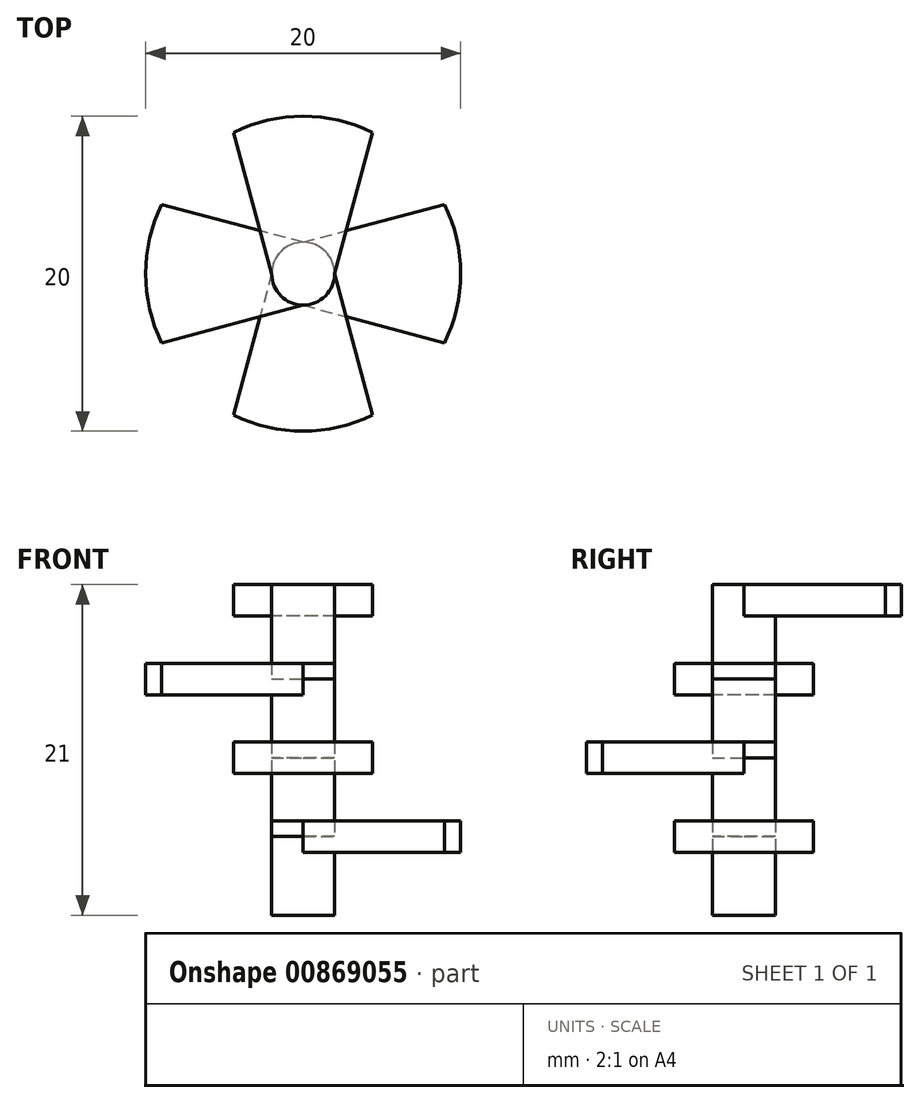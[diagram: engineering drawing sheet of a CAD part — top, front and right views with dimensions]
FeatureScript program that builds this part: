
annotation { "Feature Type Name" : "Feature", "Feature Type Description" : "" }
export const myFeature = defineFeature(function(context is Context, id is Id, definition is map)
    precondition{}
    {
        {
            var Q0;
            Q0=qCreatedBy(makeId("Top.planeOp"),FACE);
            var sketch = newSketch(context, id + "F0", { "sketchPlane" : qUnion([Q0])});
            skCircle(sketch, "E0", {"center": v(0, 0) * mm, "radius": 2 * mm});
            skCircle(sketch, "E1", {"center": v(0, 0) * mm, "radius": 10 * mm});
            skLineSegment(sketch, "E2", {"start": v(0, 2) * mm, "end": v(8.98, 4.4) * mm});
            skLineSegment(sketch, "E3", {"start": v(0, -2) * mm, "end": v(8.98, -4.4) * mm});
            skLineSegment(sketch, "E4", {"start": v(0, 0) * mm, "end": v(14.7, 0) * mm, "construction": true});
            skLineSegment(sketch, "E5", {"start": v(0, 10.76) * mm, "end": v(0, -10.34) * mm, "construction": true});
            skSolve(sketch);
        }
        {
            var Q0;
            {var subQ0=sQuery(id+"F0.wireOp",EDGE,"E2");var subQ1=sQuery(id+"F0.wireOp",EDGE,"E0");var subQ2=makeQuery(id+"F0.imprint","INTERSECT",VERTEX,{"derivedFrom":[subQ1,subQ0]});Q0=makeQuery(id+"F0.imprint","IMPRINT",FACE,{"disambiguationData":[TD([[makeQuery(id+"F0.imprint","IMPRINT",EDGE,{"disambiguationData":[TD([[subQ2,-1.0]])],"derivedFrom":subQ1}),1.0]])]});}
            var Q1;
            {var subQ0=sQuery(id+"F0.wireOp",EDGE,"E2");var subQ1=sQuery(id+"F0.wireOp",EDGE,"E0");var subQ2=makeQuery(id+"F0.imprint","INTERSECT",VERTEX,{"derivedFrom":[subQ1,subQ0]});Q1=makeQuery(id+"F0.imprint","IMPRINT",FACE,{"disambiguationData":[TD([[makeQuery(id+"F0.imprint","IMPRINT",EDGE,{"disambiguationData":[TD([[subQ2,1.0]])],"derivedFrom":subQ1}),1.0]])]});}
            var Q2;
            {var subQ0=sQuery(id+"F0.wireOp",EDGE,"E2");var subQ1=sQuery(id+"F0.wireOp",EDGE,"E0");var subQ2=makeQuery(id+"F0.imprint","INTERSECT",VERTEX,{"derivedFrom":[subQ1,subQ0]});Q2=makeQuery(id+"F0.imprint","IMPRINT",FACE,{"disambiguationData":[TD([[makeQuery(id+"F0.imprint","IMPRINT",EDGE,{"disambiguationData":[TD([[subQ2,1.0]])],"derivedFrom":subQ1}),-1.0]])]});}
            extrude(context, id + "F1", {"entities" : qUnion([Q0, Q1, Q2]), "depth" : 2 * mm, "offsetDistance" : 25 * mm});
        }
        {
            var Q0;
            {var subQ0=sQuery(id+"F0.wireOp",EDGE,"E0");var subQ1=makeQuery(id+"F0.imprint","INTERSECT",VERTEX,{"derivedFrom":[subQ0,sQuery(id+"F0.wireOp",EDGE,"E2")]});Q0=makeQuery(id+"F0.imprint","IMPRINT",FACE,{"disambiguationData":[TD([[makeQuery(id+"F0.imprint","IMPRINT",EDGE,{"disambiguationData":[TD([[subQ1,-1.0]])],"derivedFrom":subQ0}),1.0]])]});}
            extrude(context, id + "F2", {"entities" : qUnion([Q0]), "operationType" : NewBodyOperationType.ADD, "oppositeDirection" : true, "depth" : 4 * mm, "offsetDistance" : 25 * mm});
        }
        {
            var Q0;
            Q0=qCreatedBy(makeId("Right.planeOp"),FACE);
            var sketch = newSketch(context, id + "F3", { "sketchPlane" : qUnion([Q0])});
            skLineSegment(sketch, "E6", {"start": v(0, 61.65) * mm, "end": v(0, -58.63) * mm, "construction": true});
            skSolve(sketch);
        }
        {
            var Q0;
            Q0=makeQuery(id+"F1.opExtrude","SWEPT_BODY",BODY,{"disambiguationData":[OSD([sQuery(id+"F0.wireOp",EDGE,"E0"),sQuery(id+"F0.wireOp",EDGE,"E1"),sQuery(id+"F0.wireOp",EDGE,"E2"),sQuery(id+"F0.wireOp",EDGE,"E3")])]});
            var Q1;
            Q1=sQuery(id+"F3.wireOp",EDGE,"E6");
            circularPattern(context, id + "F4", {"entities" : qUnion([Q0]), "axis" : qUnion([Q1]), "angle" : 360 * degree, "instanceCount" : 4, "equalSpace" : true});
        }
        {
            var Q0;
            Q0=makeQuery(id+"F4.opPattern","COPY",BODY,{"derivedFrom":makeQuery(id+"F1.opExtrude","SWEPT_BODY",BODY,{"disambiguationData":[OSD([sQuery(id+"F0.wireOp",EDGE,"E0"),sQuery(id+"F0.wireOp",EDGE,"E1"),sQuery(id+"F0.wireOp",EDGE,"E2"),sQuery(id+"F0.wireOp",EDGE,"E3")])]}),"instanceName":"1"});
            transform(context, id + "F5", {"entities" : qUnion([Q0]), "transformType" : TransformType.TRANSLATION_3D, "dx" : 0 * mm, "dy" : 0 * mm, "dz" : 5 * mm, "makeCopy" : false});
        }
        {
            var Q0;
            Q0=makeQuery(id+"F4.opPattern","COPY",BODY,{"derivedFrom":makeQuery(id+"F1.opExtrude","SWEPT_BODY",BODY,{"disambiguationData":[OSD([sQuery(id+"F0.wireOp",EDGE,"E0"),sQuery(id+"F0.wireOp",EDGE,"E1"),sQuery(id+"F0.wireOp",EDGE,"E2"),sQuery(id+"F0.wireOp",EDGE,"E3")])]}),"instanceName":"2"});
            transform(context, id + "F6", {"entities" : qUnion([Q0]), "transformType" : TransformType.TRANSLATION_3D, "dx" : 0 * mm, "dy" : 0 * mm, "dz" : 10 * mm, "makeCopy" : false});
        }
        {
            var Q0;
            Q0=makeQuery(id+"F4.opPattern","COPY",BODY,{"derivedFrom":makeQuery(id+"F1.opExtrude","SWEPT_BODY",BODY,{"disambiguationData":[OSD([sQuery(id+"F0.wireOp",EDGE,"E0"),sQuery(id+"F0.wireOp",EDGE,"E1"),sQuery(id+"F0.wireOp",EDGE,"E2"),sQuery(id+"F0.wireOp",EDGE,"E3")])]}),"instanceName":"3"});
            transform(context, id + "F7", {"entities" : qUnion([Q0]), "transformType" : TransformType.TRANSLATION_3D, "dx" : 0 * mm, "dy" : 0 * mm, "dz" : 10 * mm, "makeCopy" : false});
        }
        {
            var Q0;
            Q0=makeQuery(id+"F4.opPattern","COPY",BODY,{"derivedFrom":makeQuery(id+"F1.opExtrude","SWEPT_BODY",BODY,{"disambiguationData":[OSD([sQuery(id+"F0.wireOp",EDGE,"E0"),sQuery(id+"F0.wireOp",EDGE,"E1"),sQuery(id+"F0.wireOp",EDGE,"E2"),sQuery(id+"F0.wireOp",EDGE,"E3")])]}),"instanceName":"3"});
            transform(context, id + "F8", {"entities" : qUnion([Q0]), "transformType" : TransformType.TRANSLATION_3D, "dx" : 0 * mm, "dy" : 0 * mm, "dz" : 5 * mm, "makeCopy" : false});
        }
    });
